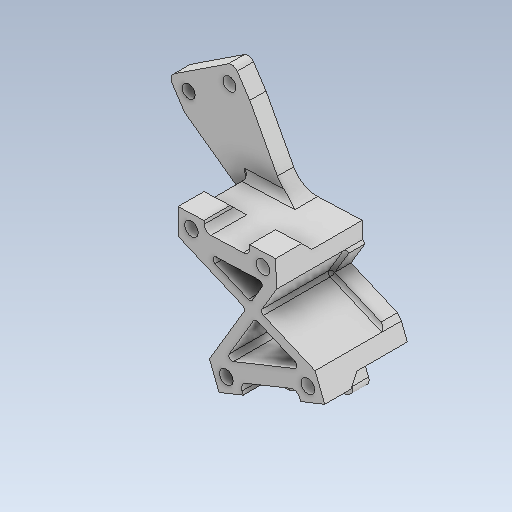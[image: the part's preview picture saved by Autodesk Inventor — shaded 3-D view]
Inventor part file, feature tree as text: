
AUTODESK INVENTOR PART (.ipt)
format: ipt  version: 2020 (Build 240168000, 168)  size: 544,256 bytes
history: native  units: mm
features: projected_geometry x15, extrude x9, sketch x9, reference x8, fillet x7, other x7, plane x1, thicken_offset x1, chamfer x1
ambient origin geometry x8: Origin, YZ Plane, XZ Plane, XY Plane, X Axis, Y Axis, Z Axis, Center Point
bodies: Solid1 (feature_tree)
feature tree (58):
  extrude  "Extrusion1"  Depth=9.0mm
  extrude  "Extrusion2"  Depth=9.0mm
  sketch  "Sketch3"  dims[d4=24.0mm d5=48.0mm]
  plane  "Work Plane1"
  extrude  "Extrusion3"  Depth=48.0mm
  thicken_offset  "Thicken1"
  extrude  "Extrusion4"  Depth=5.0mm TaperAngle=0.0deg
  extrude  "Extrusion5"  Depth=5.0mm
  chamfer  "Chamfer1"  Distance=35.0mm
  extrude  "Extrusion6"  Depth=2.0mm TaperAngle=0.0deg
  extrude  "Extrusion7"  Depth=2.0mm
  extrude  "Extrusion8"  Depth=2.0mm
  fillet  "Fillet1"  Radius=5.0mm
  extrude  "Extrusion9"  Depth=8.0mm
  fillet  "Fillet2"  Radius=8.0mm
  fillet  "Fillet3"  Radius=8.0mm
  fillet  "Fillet4"  Radius=8.0mm
  fillet  "Fillet5"  Radius=8.0mm
  fillet  "Fillet6"  Radius=8.0mm
  fillet  "Fillet7"  Radius=8.0mm
  sketch  "Sketch1"  dims[d0=60.0mm d1=9.0mm]
  reference  "Reference1"
  reference  "Reference2"
  reference  "Reference3"
  reference  "Reference4"
  reference  "Reference5"
  reference  "Reference6"
  reference  "Reference7"
  sketch  "Sketch2"  dims[d2=24.0mm d3=9.0mm]
  projected_geometry  "Projected Loop1"
  projected_geometry  "Projected Loop2"
  reference  "Reference8"
  sketch  "Sketch4"  dims[d6=5.0mm d7=0.0mm d8=5.0mm d9=0.0mm]
  projected_geometry  "Projected Loop3"
  projected_geometry  "Projected Loop4"
  sketch  "Sketch5"  dims[d10=25.0mm d11=5.0mm]
  projected_geometry  "Projected Loop5"
  projected_geometry  "Projected Loop6"
  sketch  "Sketch6"  dims[d12=35.0mm]
  projected_geometry  "Projected Loop7"
  projected_geometry  "Projected Loop8"
  sketch  "Sketch7"  dims[d13=5.0mm]
  projected_geometry  "Projected Loop9"
  projected_geometry  "Projected Loop10"
  sketch  "Sketch8"  dims[d14=5.0mm]
  projected_geometry  "Projected Loop11"
  projected_geometry  "Projected Loop12"
  sketch  "Sketch9"  dims[d15=45.0mm d16=35.0mm d17=5.0mm d18=0.0mm d19=5.0mm d20=5.0mm d21=5.0mm d22=0.0mm d23=8.0mm d24=8.0mm d25=8.0mm d26=8.0mm d27=8.0mm d28=8.0mm d29=8.0mm d30=8.0mm d31=8.0mm d32=8.0mm d33=8.0mm d34=8.0mm d35=8.0mm d36=0.0mm d37=3.0mm d38=2.0mm d39=45.0deg d40=4.2mm d41=4.2mm d42=4.2mm d43=4.2mm d44=6.0mm d45=0.0mm d46=3.0mm d47=3.0mm d48=6.0mm d49=0.0mm d50=6.0mm d51=0.0mm d52=1.0mm d53=6.0mm d54=0.0mm d55=1.0mm d56=0.5mm d57=3.0mm d58=8.0mm d59=2.0mm d60=2.0mm d61=2.0mm]
  projected_geometry  "Projected Loop13"
  projected_geometry  "Projected Loop14"
  projected_geometry  "Projected Loop15"
  parser-record x1  (decoder bookkeeping rows leaked as tree rows — omitted from the tree; the rows remain in map.json)
  other  "reducer_leg.iam"
  other  "motor_h_4:1"
  other  "end_holder_2:1"
  other  "bearing_35_44_5:1"
  other  "motor_r_1:1"
  other  "motor_h_6:1"
note: 1 file-system path scrubbed to <path> (originals preserved in map.json)
